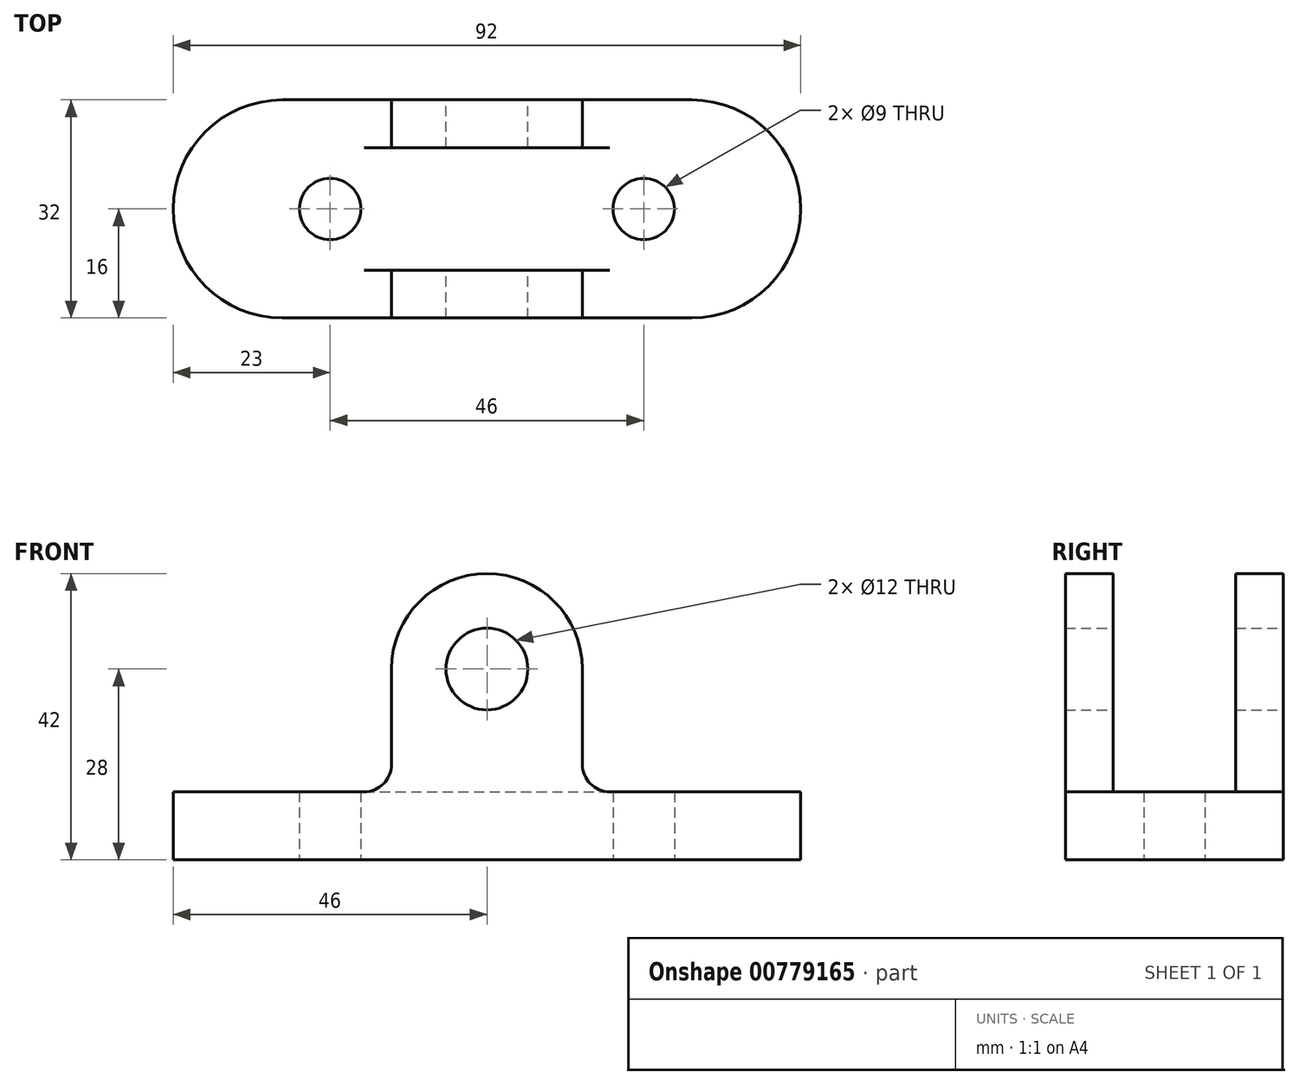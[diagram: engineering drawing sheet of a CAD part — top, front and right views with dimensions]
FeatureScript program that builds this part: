
annotation { "Feature Type Name" : "Feature", "Feature Type Description" : "" }
export const myFeature = defineFeature(function(context is Context, id is Id, definition is map)
    precondition{}
    {
        {
            var Q0;
            Q0=qCreatedBy(makeId("Top.planeOp"),FACE);
            var sketch = newSketch(context, id + "F0", { "sketchPlane" : qUnion([Q0])});
            skLineSegment(sketch, "E0.bottom", {"start": v(46, 16) * mm, "end": v(-46, 16) * mm});
            skLineSegment(sketch, "E0.top", {"start": v(46, -16) * mm, "end": v(-46, -16) * mm});
            skLineSegment(sketch, "E0.left", {"start": v(46, 16) * mm, "end": v(46, -16) * mm});
            skLineSegment(sketch, "E0.right", {"start": v(-46, 16) * mm, "end": v(-46, -16) * mm});
            skPoint(sketch, "E0.middle", {"position": v(0, 0) * mm});
            skLineSegment(sketch, "E1", {"start": v(0, 0) * mm, "end": v(46, 0) * mm});
            skLineSegment(sketch, "E2", {"start": v(0, 0) * mm, "end": v(-46, 0) * mm});
            skLineSegment(sketch, "E3", {"start": v(46, 0) * mm, "end": v(23, 0) * mm});
            skLineSegment(sketch, "E4", {"start": v(-46, 0) * mm, "end": v(-23, 0) * mm});
            skLineSegment(sketch, "E5", {"start": v(0, 0) * mm, "end": v(0, 16) * mm});
            skLineSegment(sketch, "E6", {"start": v(0, 0) * mm, "end": v(0, -16) * mm});
            skLineSegment(sketch, "E7.top", {"start": v(14, 9) * mm, "end": v(-14, 9) * mm});
            skPoint(sketch, "E7.middle", {"position": v(0, 16) * mm});
            skLineSegment(sketch, "E8.bottom", {"start": v(14, -9) * mm, "end": v(-14, -9) * mm});
            skPoint(sketch, "E8.middle", {"position": v(0, -16) * mm});
            skLineSegment(sketch, "E9", {"start": v(-14, 9) * mm, "end": v(-14, 16) * mm});
            skLineSegment(sketch, "E10", {"start": v(14, 9) * mm, "end": v(14, 16) * mm});
            skLineSegment(sketch, "E11", {"start": v(-14, -9) * mm, "end": v(-14, -16) * mm});
            skLineSegment(sketch, "E12", {"start": v(14, -9) * mm, "end": v(14, -16) * mm});
            skSolve(sketch);
        }
        {
            var Q0;
            Q0 = qSketchRegion(id + "F0", true);
            extrude(context, id + "F1", {"entities" : qUnion([Q0]), "depth" : 10 * mm, "offsetDistance" : 25 * mm});
        }
        {
            var Q0;
            Q0=makeQuery(id+"F1.opExtrude","SWEPT_EDGE",EDGE,{"disambiguationData":[OSD([sQuery(id+"F0.wireOp",EDGE,"E0.top"),sQuery(id+"F0.wireOp",EDGE,"E0.right")])]});
            var Q1;
            Q1=makeQuery(id+"F1.opExtrude","SWEPT_EDGE",EDGE,{"disambiguationData":[OSD([sQuery(id+"F0.wireOp",EDGE,"E0.bottom"),sQuery(id+"F0.wireOp",EDGE,"E0.right")])]});
            var Q2;
            Q2=makeQuery(id+"F1.opExtrude","SWEPT_EDGE",EDGE,{"disambiguationData":[OSD([sQuery(id+"F0.wireOp",EDGE,"E0.bottom"),sQuery(id+"F0.wireOp",EDGE,"E0.left")])]});
            var Q3;
            Q3=makeQuery(id+"F1.opExtrude","SWEPT_EDGE",EDGE,{"disambiguationData":[OSD([sQuery(id+"F0.wireOp",EDGE,"E0.top"),sQuery(id+"F0.wireOp",EDGE,"E0.left")])]});
            fillet(context, id + "F2", {"entities" : qUnion([Q0, Q1, Q2, Q3]), "radius" : 16 * mm, "tangentPropagation" : true, "allowEdgeOverflow" : false});
        }
        {
            var Q0;
            Q0=sQuery(id+"F0.wireOp",VERTEX,"E3.end");
            var Q1;
            Q1=sQuery(id+"F0.wireOp",VERTEX,"E4.end");
            var Q2;
            Q2=makeQuery(id+"F1.opExtrude","SWEPT_BODY",BODY,{"disambiguationData":[OSD([sQuery(id+"F0.wireOp",EDGE,"E0.bottom"),sQuery(id+"F0.wireOp",EDGE,"E0.top"),sQuery(id+"F0.wireOp",EDGE,"E0.left"),sQuery(id+"F0.wireOp",EDGE,"E0.right")])]});
            hole(context, id + "F3", {"style" : HoleStyle.SIMPLE, "endStyle" : HoleEndStyle.THROUGH, "oppositeDirection" : true, "holeDiameter" : 9 * mm, "majorDiameter" : 5 * mm, "isTappedThrough" : true, "tappedDepth" : 12 * mm, "tapClearance" : 3, "startFromSketch" : true, "locations" : qUnion([Q0, Q1]), "scope" : qUnion([Q2])});
        }
        {
            var Q0;
            {var subQ3=sQuery(id+"F0.wireOp",EDGE,"E11");Q0=makeQuery(id+"F0.imprint","IMPRINT",FACE,{"disambiguationData":[TD([[makeQuery(id+"F0.imprint","IMPRINT",EDGE,{"derivedFrom":subQ3}),1.0]])]});}
            var Q1;
            {var subQ3=sQuery(id+"F0.wireOp",EDGE,"E12");Q1=makeQuery(id+"F0.imprint","IMPRINT",FACE,{"disambiguationData":[TD([[makeQuery(id+"F0.imprint","IMPRINT",EDGE,{"derivedFrom":subQ3}),-1.0]])]});}
            var Q2;
            {var subQ3=sQuery(id+"F0.wireOp",EDGE,"E9");Q2=makeQuery(id+"F0.imprint","IMPRINT",FACE,{"disambiguationData":[TD([[makeQuery(id+"F0.imprint","IMPRINT",EDGE,{"derivedFrom":subQ3}),-1.0]])]});}
            var Q3;
            {var subQ3=sQuery(id+"F0.wireOp",EDGE,"E10");Q3=makeQuery(id+"F0.imprint","IMPRINT",FACE,{"disambiguationData":[TD([[makeQuery(id+"F0.imprint","IMPRINT",EDGE,{"derivedFrom":subQ3}),1.0]])]});}
            extrude(context, id + "F4", {"entities" : qUnion([Q0, Q1, Q2, Q3]), "operationType" : NewBodyOperationType.ADD, "depth" : 42 * mm, "offsetDistance" : 25 * mm});
        }
        {
            var Q0;
            Q0=makeQuery(id+"F4.boolean.opBoolean","INTERSECT",EDGE,{"derivedFrom":[makeQuery(id+"F1.opExtrude","CAP_FACE",FACE,{"disambiguationData":[OSD([sQuery(id+"F0.wireOp",EDGE,"E0.bottom"),sQuery(id+"F0.wireOp",EDGE,"E0.top"),sQuery(id+"F0.wireOp",EDGE,"E0.left"),sQuery(id+"F0.wireOp",EDGE,"E0.right")])],"isStart":false}),makeQuery(id+"F4.opExtrude","SWEPT_FACE",FACE,{"disambiguationData":[OSD([sQuery(id+"F0.wireOp",EDGE,"E10")])]})]});
            var Q1;
            Q1=makeQuery(id+"F4.boolean.opBoolean","INTERSECT",EDGE,{"derivedFrom":[makeQuery(id+"F1.opExtrude","CAP_FACE",FACE,{"disambiguationData":[OSD([sQuery(id+"F0.wireOp",EDGE,"E0.bottom"),sQuery(id+"F0.wireOp",EDGE,"E0.top"),sQuery(id+"F0.wireOp",EDGE,"E0.left"),sQuery(id+"F0.wireOp",EDGE,"E0.right")])],"isStart":false}),makeQuery(id+"F4.opExtrude","SWEPT_FACE",FACE,{"disambiguationData":[OSD([sQuery(id+"F0.wireOp",EDGE,"E12")])]})]});
            var Q2;
            Q2=makeQuery(id+"F4.boolean.opBoolean","INTERSECT",EDGE,{"derivedFrom":[makeQuery(id+"F1.opExtrude","CAP_FACE",FACE,{"disambiguationData":[OSD([sQuery(id+"F0.wireOp",EDGE,"E0.bottom"),sQuery(id+"F0.wireOp",EDGE,"E0.top"),sQuery(id+"F0.wireOp",EDGE,"E0.left"),sQuery(id+"F0.wireOp",EDGE,"E0.right")])],"isStart":false}),makeQuery(id+"F4.opExtrude","SWEPT_FACE",FACE,{"disambiguationData":[OSD([sQuery(id+"F0.wireOp",EDGE,"E9")])]})]});
            var Q3;
            Q3=makeQuery(id+"F4.boolean.opBoolean","INTERSECT",EDGE,{"derivedFrom":[makeQuery(id+"F1.opExtrude","CAP_FACE",FACE,{"disambiguationData":[OSD([sQuery(id+"F0.wireOp",EDGE,"E0.bottom"),sQuery(id+"F0.wireOp",EDGE,"E0.top"),sQuery(id+"F0.wireOp",EDGE,"E0.left"),sQuery(id+"F0.wireOp",EDGE,"E0.right")])],"isStart":false}),makeQuery(id+"F4.opExtrude","SWEPT_FACE",FACE,{"disambiguationData":[OSD([sQuery(id+"F0.wireOp",EDGE,"E11")])]})]});
            fillet(context, id + "F5", {"entities" : qUnion([Q0, Q1, Q2, Q3]), "radius" : 4 * mm, "tangentPropagation" : true, "allowEdgeOverflow" : false});
        }
        {
            var Q0;
            {var subQ0=sQuery(id+"F0.wireOp",EDGE,"E0.bottom");Q0=makeQuery(id+"F4.boolean.opBoolean","MERGE",FACE,{"derivedFrom":[makeQuery(id+"F1.opExtrude","SWEPT_FACE",FACE,{"disambiguationData":[OSD([subQ0])]}),makeQuery(id+"F4.opExtrude","SWEPT_FACE",FACE,{"disambiguationData":[OSD([subQ0])]})]});}
            var sketch = newSketch(context, id + "F6", { "sketchPlane" : qUnion([Q0])});
            skPoint(sketch, "E13", {"position": v(0, 28) * mm});
            skCircle(sketch, "E14", {"center": v(0, 28) * mm, "radius": 14 * mm});
            skSolve(sketch);
        }
        {
            var Q0;
            Q0=sQuery(id+"F6.wireOp",VERTEX,"E13");
            var Q1;
            Q1=makeQuery(id+"F1.opExtrude","SWEPT_BODY",BODY,{"disambiguationData":[OSD([sQuery(id+"F0.wireOp",EDGE,"E0.bottom"),sQuery(id+"F0.wireOp",EDGE,"E0.top"),sQuery(id+"F0.wireOp",EDGE,"E0.left"),sQuery(id+"F0.wireOp",EDGE,"E0.right")])]});
            hole(context, id + "F7", {"style" : HoleStyle.SIMPLE, "endStyle" : HoleEndStyle.THROUGH, "holeDiameter" : 12 * mm, "majorDiameter" : 5 * mm, "isTappedThrough" : true, "tappedDepth" : 12 * mm, "tapClearance" : 3, "startFromSketch" : true, "locations" : qUnion([Q0]), "scope" : qUnion([Q1])});
        }
        {
            var Q0;
            Q0=makeQuery(id+"F4.opExtrude","CAP_EDGE",EDGE,{"disambiguationData":[OSD([sQuery(id+"F0.wireOp",EDGE,"E10")])],"isStart":false});
            var Q1;
            Q1=makeQuery(id+"F4.opExtrude","CAP_EDGE",EDGE,{"disambiguationData":[OSD([sQuery(id+"F0.wireOp",EDGE,"E9")])],"isStart":false});
            var Q2;
            Q2=makeQuery(id+"F4.opExtrude","CAP_EDGE",EDGE,{"disambiguationData":[OSD([sQuery(id+"F0.wireOp",EDGE,"E12")])],"isStart":false});
            var Q3;
            Q3=makeQuery(id+"F4.opExtrude","CAP_EDGE",EDGE,{"disambiguationData":[OSD([sQuery(id+"F0.wireOp",EDGE,"E11")])],"isStart":false});
            fillet(context, id + "F8", {"entities" : qUnion([Q0, Q1, Q2, Q3]), "radius" : 14 * mm, "tangentPropagation" : true, "allowEdgeOverflow" : false});
        }
    });
